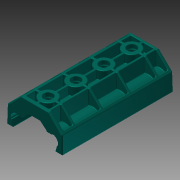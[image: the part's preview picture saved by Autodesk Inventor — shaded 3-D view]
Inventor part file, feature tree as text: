
AUTODESK INVENTOR PART (.ipt)
format: ipt  version: 2013 (Build 170138000, 138)  size: 1,816,576 bytes
history: native  units: in
note: dims shown in document units (in); Inventor stores cm internally (conversion verified against a paired STEP export)
features: fillet x37, sketch x10, extrude x9, projected_geometry x7, pattern_linear x5, plane x3, chamfer x3, split x2, hole x1
ambient origin geometry x8: Origin, YZ Plane, XZ Plane, XY Plane, X Axis, Y Axis, Z Axis, Center Point
bodies: Solid1 (feature_tree)
feature tree (77):
  extrude  "Extrusion1"  Depth=0.0067in
  plane  "Work Plane1"
  split  "Split1"
  plane  "Work Plane2"
  split  "Split2"
  plane  "Work Plane3"
  extrude  "Extrusion2"  Depth=1.875in TaperAngle=0.0deg
  extrude  "Extrusion3"  Depth=0.304in
  pattern_linear  "Rectangular Pattern1"  Count1=4 Spacing1=0.5in
  extrude  "Extrusion4"  Depth=0.0625in TaperAngle=0.0deg
  extrude  "Extrusion5"  Depth=0.125in TaperAngle=0.0deg
  pattern_linear  "Rectangular Pattern2"  Count1=4 Spacing1=0.5in
  extrude  "Extrusion6"  Depth=0.5in TaperAngle=0.0deg
  extrude  "Extrusion7"  Depth=0.012in
  pattern_linear  "Rectangular Pattern3"  Spacing1=0.012in  [1 undecoded]
  fillet  "Fillet1"  Radius=0.012in
  fillet  "Fillet2"  Radius=0.012in
  fillet  "Fillet3"  Radius=0.012in
  fillet  "Fillet4"  Radius=0.012in
  fillet  "Fillet5"  Radius=0.012in
  fillet  "Fillet8"  Radius=0.012in
  fillet  "Fillet10"  Radius=0.012in
  fillet  "Fillet11"  Radius=0.012in
  fillet  "Fillet12"  Radius=0.012in
  fillet  "Fillet13"  Radius=0.012in
  fillet  "Fillet14"  Radius=0.012in
  fillet  "Fillet15"  Radius=0.012in
  fillet  "Fillet16"  Radius=0.012in
  fillet  "Fillet18"  Radius=0.1875in
  fillet  "Fillet20"  Radius=0.5in
  fillet  "Fillet21"  Radius=1.5748in
  fillet  "Fillet22"  Radius=0.012in
  extrude  "Extrusion9"  Depth=0.012in
  extrude  "Extrusion10"  Depth=0.012in
  pattern_linear  "Rectangular Pattern4"  Spacing1=0.012in  [1 undecoded]
  fillet  "Fillet29"  Radius=0.012in
  fillet  "Fillet30"  Radius=0.012in
  fillet  "Fillet31"  Radius=0.012in
  fillet  "Fillet32"  Radius=0.012in
  fillet  "Fillet33"  Radius=0.012in
  fillet  "Fillet34"  Radius=0.012in
  fillet  "Fillet35"  Radius=0.012in
  fillet  "Fillet36"  Radius=0.012in
  fillet  "Fillet37"  Radius=0.012in
  fillet  "Fillet38"  Radius=0.012in
  fillet  "Fillet39"  Radius=0.012in
  fillet  "Fillet40"  Radius=0.012in
  fillet  "Fillet41"  Radius=0.012in
  fillet  "Fillet42"  Radius=0.012in
  fillet  "Fillet43"  Radius=0.012in
  fillet  "Fillet44"  Radius=0.012in
  fillet  "Fillet45"  Radius=0.0095in
  fillet  "Fillet46"  Radius=1.5748in
  fillet  "Fillet47"  Radius=0.017in
  fillet  "Fillet48"  Radius=0.017in
  hole  "Hole1"  [1 undecoded]
  chamfer  "Chamfer1"  [1 undecoded]
  pattern_linear  "Rectangular Pattern5"  [2 undecoded]
  chamfer  "Chamfer2"  [1 undecoded]
  chamfer  "Chamfer3"  [1 undecoded]
  sketch  "Sketch1"  dims[d0=2.0in d1=0.0in d3=0.0067in]
  sketch  "Sketch5"  dims[d4=0.0067in d13=1.875in d14=0.0in]
  projected_geometry  "Projected Loop1"
  sketch  "Sketch6"  dims[d15=0.24in d16=0.304in]
  sketch  "Sketch7"  dims[d17=0.125in d18=0.0in d19=1.5748in d21=0.5in]
  projected_geometry  "Projected Loop2"
  projected_geometry  "Projected Loop3"
  projected_geometry  "Projected Loop4"
  projected_geometry  "Projected Loop5"
  sketch  "Sketch8"  dims[d22=0.04in d23=0.02in d24=0.0625in d25=0.0in]
  sketch  "Sketch9"  dims[d26=0.04in d27=0.02in d28=0.125in d29=0.0in d30=1.5748in d32=0.5in]
  projected_geometry  "Projected Loop6"
  sketch  "Sketch10"  dims[d33=0.125in d34=0.0in d35=0.5in d36=0.0in]
  sketch  "Sketch12"  dims[d37=1.5748in d39=0.5in d40=0.012in]
  sketch  "Sketch13"  dims[d41=0.012in]
  projected_geometry  "Projected Loop8"
  sketch  "Sketch14"  dims[d42=0.012in d43=0.012in d44=0.012in d47=0.012in d49=0.012in d50=0.012in d51=0.012in d52=0.012in d53=0.012in d54=0.012in d55=0.012in d57=0.012in d59=0.012in d60=0.012in d61=0.012in d70=0.1875in d71=0.0in d72=0.5in d73=0.0in d74=1.5748in d76=0.5in d77=0.012in d78=0.012in d79=0.012in d80=0.012in d81=0.012in d82=0.012in d83=0.012in d84=0.012in d85=0.012in d86=0.012in d87=0.012in d88=0.012in d89=0.012in d90=0.012in d91=0.012in d92=0.012in d93=0.012in d94=0.012in d95=0.012in d96=0.012in d97=0.146in d98=0.75in d99=0.165in d100=0.066in d101=0.5635in d102=1.0in d103=0.8108in d104=0.0095in d105=0.125in d106=120.0deg d107=1.5748in d109=0.5in d110=0.017in d111=0.125in d112=45.0deg d113=0.017in d114=0.125in d115=45.0deg]
note: 8 required parameter values undecoded (feature->parameter linkage not recoverable at this tier; creation-order binding heuristic only, values carry confidence <= 0.55)
